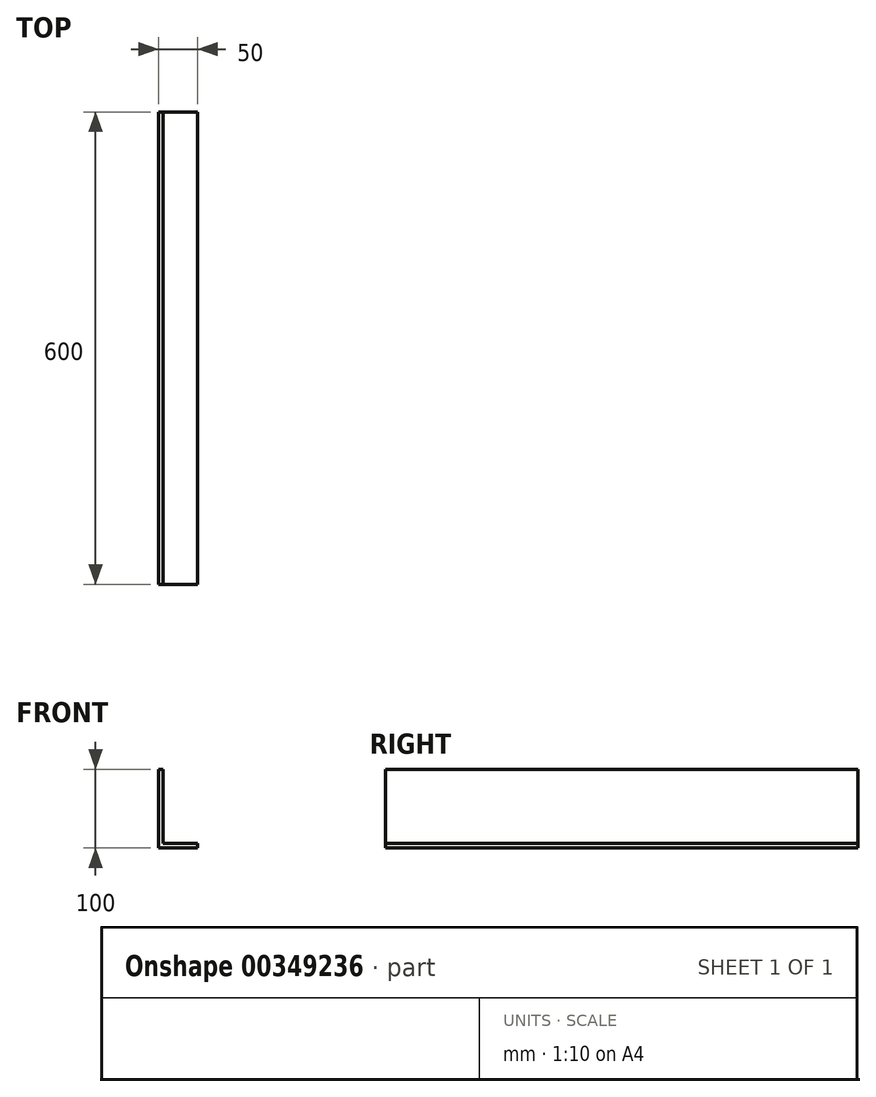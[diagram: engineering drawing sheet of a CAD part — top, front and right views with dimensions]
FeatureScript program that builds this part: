
annotation { "Feature Type Name" : "Feature", "Feature Type Description" : "" }
export const myFeature = defineFeature(function(context is Context, id is Id, definition is map)
    precondition{}
    {
        {
            var Q0;
            Q0=qCreatedBy(makeId("Front.planeOp"),FACE);
            var sketch = newSketch(context, id + "F0", { "sketchPlane" : qUnion([Q0])});
            skLineSegment(sketch, "E0", {"start": v(0, -51.28) * mm, "end": v(-50, -51.28) * mm});
            skLineSegment(sketch, "E1", {"start": v(-50, -51.28) * mm, "end": v(-50, 48.72) * mm});
            skLineSegment(sketch, "E2", {"start": v(-50, 48.72) * mm, "end": v(-44, 48.72) * mm});
            skLineSegment(sketch, "E3", {"start": v(-44, 48.72) * mm, "end": v(-44, -45.28) * mm});
            skLineSegment(sketch, "E4", {"start": v(-44, -45.28) * mm, "end": v(0, -45.28) * mm});
            skLineSegment(sketch, "E5", {"start": v(0, -45.28) * mm, "end": v(0, -51.28) * mm});
            skSolve(sketch);
        }
        {
            var Q0;
            Q0 = qSketchRegion(id + "F0", true);
            extrude(context, id + "F1", {"entities" : qUnion([Q0]), "depth" : 600 * mm});
        }
    });
